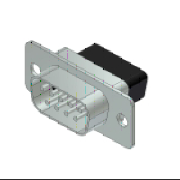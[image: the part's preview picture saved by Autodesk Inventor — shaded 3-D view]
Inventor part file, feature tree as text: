
AUTODESK INVENTOR PART (.ipt)
format: ipt  version: 2017 (Build 210142000, 142)  size: 532,480 bytes
history: native  units: in
note: dims shown in document units (in); Inventor stores cm internally (conversion verified against a paired STEP export)
features: extrude x9, sketch x7, projected_geometry x1
ambient origin geometry x8: Origin, YZ Plane, XZ Plane, XY Plane, X Axis, Y Axis, Z Axis, Center Point
bodies: Solid1 (feature_tree)
feature tree (17):
  extrude  "Extrusion1"  Depth=0.218in TaperAngle=0.0deg
  extrude  "Extrusion2"  Depth=0.283in TaperAngle=0.0deg
  extrude  "Extrusion3"  Depth=0.062in
  extrude  "Extrusion4"  Depth=0.0687in
  sketch  "Sketch14"  dims[d122=2.28in d124=2.729in]
  extrude  "Extrusion15"  Depth=2.729in
  sketch  "Sketch15"  dims[d125=0.496in d126=0.062in]
  extrude  "Extrusion16"  Depth=0.062in
  extrude  "Extrusion17"  Depth=0.311in
  extrude  "Extrusion18"  Depth=0.037in
  extrude  "Extrusion19"  Depth=0.037in
  sketch  "Sketch16"  dims[d127=0.1in d129=0.311in d131=0.0687in d132=0.0687in d133=2.159in d134=0.12in d135=2.5in d136=0.282in d137=0.048in d139=0.0687in d140=0.0687in d141=2.135in d144=0.087in d147=1.0in d148=0.0in d149=0.042in d152=0.2in d153=0.0in d157=7.4803in d159=0.108in d162=0.087in d165=1.0in d166=0.0in d171=0.2in d172=0.0in d176=7.0866in d178=0.108in d181=0.0038in d182=0.2749in d183=0.0051in d184=0.0038in d185=0.03in d186=0.0249in d187=0.0058in d188=0.0058in d189=0.2749in d190=0.9619in d193=0.001in d194=0.0in d198=0.0196in d199=0.111in d200=0.0196in d201=0.111in d204=90.0deg d205=0.6871in d206=90.0deg d207=0.5497in d208=90.0deg d209=0.5497in d210=0.7244in d211=0.6201in d212=90.0deg d213=0.6871in d214=90.0deg d215=0.5497in d216=90.0deg d217=0.5497in d218=90.0deg d219=0.6871in d292=0.016in d293=0.016in d294=0.016in d295=0.0545in d296=0.0547in d297=0.042in d298=0.037in d299=0.063in d300=0.037in d301=0.0015in d302=0.0005in d303=0.0359in d304=0.0005in d380=0.149in]
  sketch  "Sketch1"  dims[d4=0.03in d5=0.0in d9=0.218in d10=0.0in]
  sketch  "Sketch2"  dims[d14=0.155in d15=0.0in d19=0.283in d20=0.0in]
  sketch  "Sketch3"  dims[d114=0.433in d119=0.062in]
  sketch  "Sketch4"  dims[d120=0.0687in d121=0.0687in]
  projected_geometry  "Projected Loop2"
